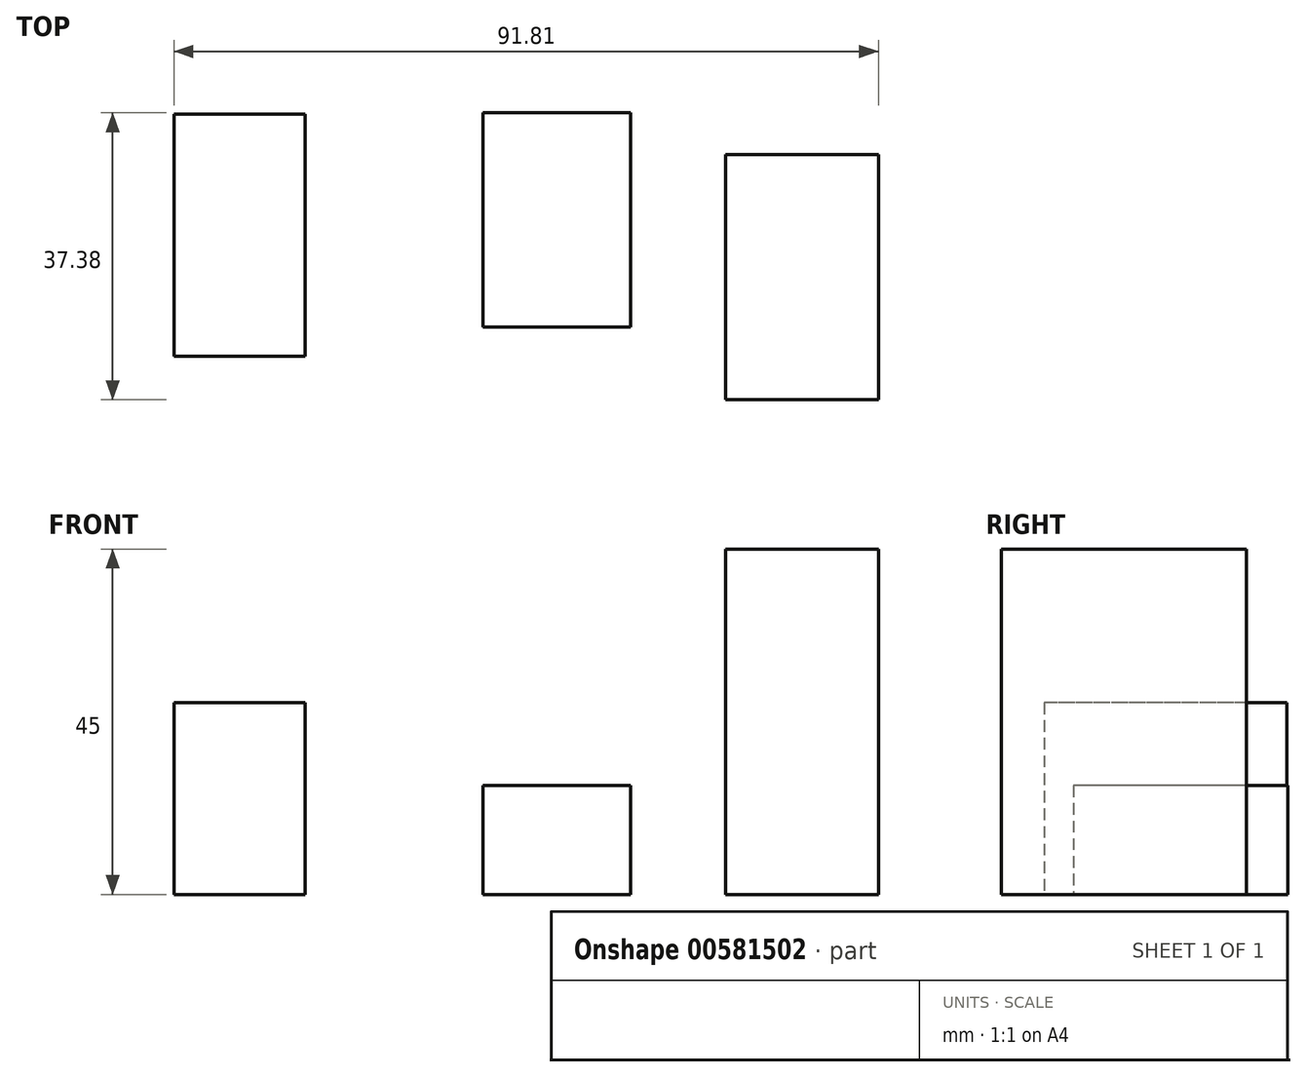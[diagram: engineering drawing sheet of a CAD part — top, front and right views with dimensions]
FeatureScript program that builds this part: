
annotation { "Feature Type Name" : "Feature", "Feature Type Description" : "" }
export const myFeature = defineFeature(function(context is Context, id is Id, definition is map)
    precondition{}
    {
        {
            var Q0;
            Q0=qCreatedBy(makeId("Top.planeOp"),FACE);
            var sketch = newSketch(context, id + "F0", { "sketchPlane" : qUnion([Q0])});
            skLineSegment(sketch, "E0.bottom", {"start": v(-33.84, 19.32) * mm, "end": v(-16.78, 19.32) * mm});
            skLineSegment(sketch, "E0.top", {"start": v(-33.84, -12.25) * mm, "end": v(-16.78, -12.25) * mm});
            skLineSegment(sketch, "E0.left", {"start": v(-33.84, 19.32) * mm, "end": v(-33.84, -12.25) * mm});
            skLineSegment(sketch, "E0.right", {"start": v(-16.78, 19.32) * mm, "end": v(-16.78, -12.25) * mm});
            skLineSegment(sketch, "E1.bottom", {"start": v(6.44, 19.5) * mm, "end": v(25.68, 19.5) * mm});
            skLineSegment(sketch, "E1.top", {"start": v(6.44, -8.44) * mm, "end": v(25.68, -8.44) * mm});
            skLineSegment(sketch, "E1.left", {"start": v(6.44, 19.5) * mm, "end": v(6.44, -8.44) * mm});
            skLineSegment(sketch, "E1.right", {"start": v(25.68, 19.5) * mm, "end": v(25.68, -8.44) * mm});
            skLineSegment(sketch, "E2.bottom", {"start": v(38.01, 14.06) * mm, "end": v(57.97, 14.06) * mm});
            skLineSegment(sketch, "E2.top", {"start": v(38.01, -17.87) * mm, "end": v(57.97, -17.87) * mm});
            skLineSegment(sketch, "E2.left", {"start": v(38.01, 14.06) * mm, "end": v(38.01, -17.87) * mm});
            skLineSegment(sketch, "E2.right", {"start": v(57.97, 14.06) * mm, "end": v(57.97, -17.87) * mm});
            skSolve(sketch);
        }
        {
            var Q0;
            Q0=makeQuery(id+"F0.imprint","IMPRINT",FACE,{"disambiguationData":[TD([[makeQuery(id+"F0.imprint","IMPRINT",EDGE,{"derivedFrom":sQuery(id+"F0.wireOp",EDGE,"E0.bottom")}),-1.0]])]});
            extrude(context, id + "F1", {"entities" : qUnion([Q0]), "depth" : 25 * mm, "offsetDistance" : 25 * mm});
        }
        {
            var Q0;
            Q0=makeQuery(id+"F0.imprint","IMPRINT",FACE,{"disambiguationData":[TD([[makeQuery(id+"F0.imprint","IMPRINT",EDGE,{"derivedFrom":sQuery(id+"F0.wireOp",EDGE,"E1.bottom")}),-1.0]])]});
            extrude(context, id + "F2", {"entities" : qUnion([Q0]), "depth" : 14.2 * mm, "offsetDistance" : 25 * mm});
        }
        {
            var Q0;
            Q0=makeQuery(id+"F0.imprint","IMPRINT",FACE,{"disambiguationData":[TD([[makeQuery(id+"F0.imprint","IMPRINT",EDGE,{"derivedFrom":sQuery(id+"F0.wireOp",EDGE,"E2.bottom")}),-1.0]])]});
            extrude(context, id + "F3", {"entities" : qUnion([Q0]), "depth" : 45 * mm, "offsetDistance" : 25 * mm});
        }
    });
